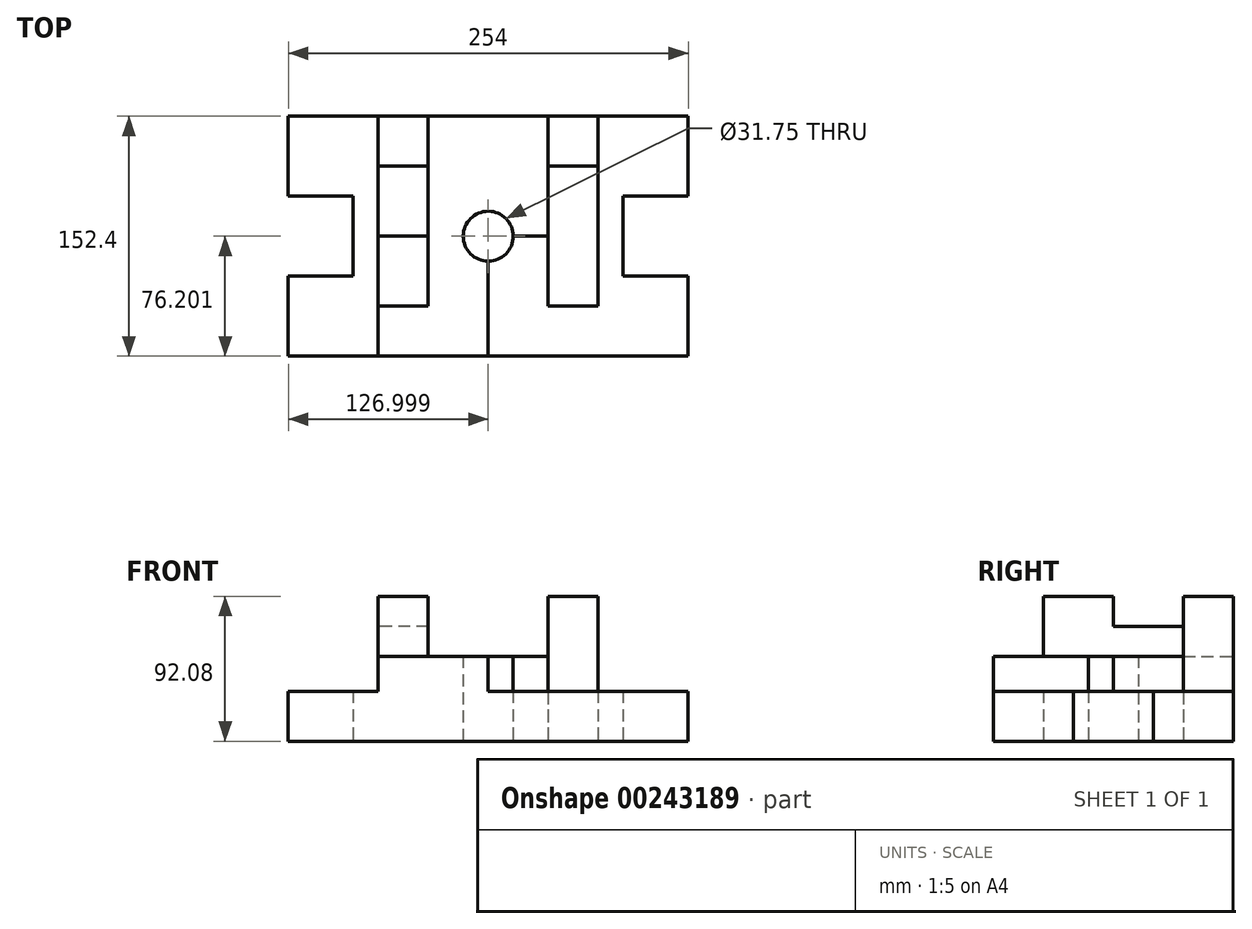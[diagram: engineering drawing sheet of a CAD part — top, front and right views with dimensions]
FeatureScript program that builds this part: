
annotation { "Feature Type Name" : "Feature", "Feature Type Description" : "" }
export const myFeature = defineFeature(function(context is Context, id is Id, definition is map)
    precondition{}
    {
        {
            var Q0;
            Q0=qCreatedBy(makeId("Top.planeOp"),FACE);
            var sketch = newSketch(context, id + "F0", { "sketchPlane" : qUnion([Q0])});
            skLineSegment(sketch, "E0.bottom", {"start": v(84.48, -54.02) * mm, "end": v(-42.52, -54.02) * mm});
            skLineSegment(sketch, "E0.top", {"start": v(84.48, -3.22) * mm, "end": v(43.2, -3.22) * mm});
            skLineSegment(sketch, "E0.left", {"start": v(84.48, -54.02) * mm, "end": v(84.48, -3.22) * mm});
            skLineSegment(sketch, "E0.right", {"start": v(-42.52, -54.02) * mm, "end": v(-42.52, -3.22) * mm});
            skLineSegment(sketch, "E1.top", {"start": v(-42.52, 22.18) * mm, "end": v(43.2, 22.18) * mm});
            skLineSegment(sketch, "E1.left", {"start": v(-42.52, -3.22) * mm, "end": v(-42.52, 22.18) * mm});
            skLineSegment(sketch, "E1.right", {"start": v(43.2, -3.22) * mm, "end": v(43.2, 22.18) * mm});
            skLineSegment(sketch, "E2.bottom", {"start": v(-42.52, -54.02) * mm, "end": v(27.33, -54.02) * mm});
            skLineSegment(sketch, "E2.top", {"start": v(-42.52, 22.18) * mm, "end": v(27.33, 22.18) * mm});
            skLineSegment(sketch, "E2.left", {"start": v(-42.52, -54.02) * mm, "end": v(-42.52, 22.18) * mm});
            skLineSegment(sketch, "E2.right", {"start": v(27.33, -54.02) * mm, "end": v(27.33, 22.18) * mm});
            skLineSegment(sketch, "E3.bottom", {"start": v(27.33, -54.02) * mm, "end": v(-4.42, -54.02) * mm});
            skLineSegment(sketch, "E3.top", {"start": v(27.33, -22.27) * mm, "end": v(-4.42, -22.27) * mm});
            skLineSegment(sketch, "E3.left", {"start": v(27.33, -54.02) * mm, "end": v(27.33, -22.27) * mm});
            skLineSegment(sketch, "E3.right", {"start": v(-4.42, -54.02) * mm, "end": v(-4.42, -22.27) * mm});
            skLineSegment(sketch, "E4.MirrorCS", {"start": v(84.48, 47.58) * mm, "end": v(43.2, 47.58) * mm});
            skLineSegment(sketch, "E5.MirrorCS", {"start": v(27.33, 66.63) * mm, "end": v(-4.42, 66.63) * mm});
            skLineSegment(sketch, "E6.MirrorCS", {"start": v(-42.52, 47.58) * mm, "end": v(-42.52, 22.18) * mm});
            skLineSegment(sketch, "E7.MirrorCS", {"start": v(-42.52, 98.38) * mm, "end": v(-42.52, 47.58) * mm});
            skLineSegment(sketch, "E8.MirrorCS", {"start": v(27.33, 98.38) * mm, "end": v(27.33, 66.63) * mm});
            skLineSegment(sketch, "E9.MirrorCS", {"start": v(-4.42, 98.38) * mm, "end": v(-4.42, 66.63) * mm});
            skLineSegment(sketch, "E10.MirrorCS", {"start": v(27.33, 98.38) * mm, "end": v(-4.42, 98.38) * mm});
            skLineSegment(sketch, "E11.MirrorCS", {"start": v(43.2, 47.58) * mm, "end": v(43.2, 22.18) * mm});
            skLineSegment(sketch, "E12.MirrorCS", {"start": v(84.48, 98.38) * mm, "end": v(-42.52, 98.38) * mm});
            skLineSegment(sketch, "E13.MirrorCS", {"start": v(27.33, 98.38) * mm, "end": v(27.33, 22.18) * mm});
            skLineSegment(sketch, "E14.MirrorCS", {"start": v(-42.52, 98.38) * mm, "end": v(27.33, 98.38) * mm});
            skLineSegment(sketch, "E15.MirrorCS", {"start": v(-42.52, 98.38) * mm, "end": v(-42.52, 22.18) * mm});
            skLineSegment(sketch, "E16.MirrorCS", {"start": v(84.48, 98.38) * mm, "end": v(84.48, 47.58) * mm});
            skLineSegment(sketch, "E17.MirrorCS", {"start": v(-169.52, 47.58) * mm, "end": v(-128.25, 47.58) * mm});
            skLineSegment(sketch, "E18.MirrorCS", {"start": v(-42.52, 22.18) * mm, "end": v(-112.37, 22.18) * mm});
            skLineSegment(sketch, "E19.MirrorCS", {"start": v(-112.37, 98.38) * mm, "end": v(-80.62, 98.38) * mm});
            skLineSegment(sketch, "E20.MirrorCS", {"start": v(-112.37, 66.63) * mm, "end": v(-80.62, 66.63) * mm});
            skLineSegment(sketch, "E21.MirrorCS", {"start": v(-42.52, 22.18) * mm, "end": v(-128.25, 22.18) * mm});
            skLineSegment(sketch, "E22.MirrorCS", {"start": v(-112.37, -54.02) * mm, "end": v(-112.37, -22.27) * mm});
            skLineSegment(sketch, "E23.MirrorCS", {"start": v(-42.52, 98.38) * mm, "end": v(-112.37, 98.38) * mm});
            skLineSegment(sketch, "E24.MirrorCS", {"start": v(-112.37, -54.02) * mm, "end": v(-112.37, 22.18) * mm});
            skLineSegment(sketch, "E25.MirrorCS", {"start": v(-169.52, 98.38) * mm, "end": v(-169.52, 47.58) * mm});
            skLineSegment(sketch, "E26.MirrorCS", {"start": v(-80.62, 98.38) * mm, "end": v(-80.62, 66.63) * mm});
            skLineSegment(sketch, "E27.MirrorCS", {"start": v(-169.52, 98.38) * mm, "end": v(-42.52, 98.38) * mm});
            skLineSegment(sketch, "E28.MirrorCS", {"start": v(-112.37, -54.02) * mm, "end": v(-80.62, -54.02) * mm});
            skLineSegment(sketch, "E29.MirrorCS", {"start": v(-112.37, 98.38) * mm, "end": v(-112.37, 22.18) * mm});
            skLineSegment(sketch, "E30.MirrorCS", {"start": v(-112.37, -22.27) * mm, "end": v(-80.62, -22.27) * mm});
            skLineSegment(sketch, "E31.MirrorCS", {"start": v(-80.62, -54.02) * mm, "end": v(-80.62, -22.27) * mm});
            skLineSegment(sketch, "E32.MirrorCS", {"start": v(-42.52, -54.02) * mm, "end": v(-112.37, -54.02) * mm});
            skLineSegment(sketch, "E33.MirrorCS", {"start": v(-169.52, -54.02) * mm, "end": v(-42.52, -54.02) * mm});
            skLineSegment(sketch, "E34.MirrorCS", {"start": v(-128.25, 47.58) * mm, "end": v(-128.25, 22.18) * mm});
            skLineSegment(sketch, "E35.MirrorCS", {"start": v(-169.52, -3.22) * mm, "end": v(-128.25, -3.22) * mm});
            skLineSegment(sketch, "E36.MirrorCS", {"start": v(-128.25, -3.22) * mm, "end": v(-128.25, 22.18) * mm});
            skLineSegment(sketch, "E37.MirrorCS", {"start": v(-169.52, -54.02) * mm, "end": v(-169.52, -3.22) * mm});
            skLineSegment(sketch, "E38.MirrorCS", {"start": v(-112.37, 98.38) * mm, "end": v(-112.37, 66.63) * mm});
            skCircle(sketch, "E39", {"center": v(-42.52, 22.18) * mm, "radius": 15.88 * mm});
            skLineSegment(sketch, "E40.left", {"start": v(-112.37, 66.63) * mm, "end": v(-112.37, -22.27) * mm});
            skLineSegment(sketch, "E40.right", {"start": v(-80.62, 66.63) * mm, "end": v(-80.62, -22.27) * mm});
            skLineSegment(sketch, "E41.bottom", {"start": v(-4.42, 66.63) * mm, "end": v(27.33, 66.63) * mm});
            skLineSegment(sketch, "E41.top", {"start": v(-4.42, -22.27) * mm, "end": v(27.33, -22.27) * mm});
            skLineSegment(sketch, "E41.left", {"start": v(-4.42, 66.63) * mm, "end": v(-4.42, -22.27) * mm});
            skLineSegment(sketch, "E41.right", {"start": v(27.33, 66.63) * mm, "end": v(27.33, -22.27) * mm});
            skSolve(sketch);
        }
        {
            var Q0;
            Q0=makeQuery(id+"F0.imprint","IMPRINT",FACE,{"disambiguationData":[TD([[makeQuery(id+"F0.imprint","IMPRINT",EDGE,{"derivedFrom":sQuery(id+"F0.wireOp",EDGE,"E3.bottom")}),-1.0]])]});
            var Q1;
            {var subQ0=sQuery(id+"F0.wireOp",EDGE,"E9.MirrorCS");Q1=makeQuery(id+"F0.imprint","IMPRINT",FACE,{"disambiguationData":[TD([[makeQuery(id+"F0.imprint","IMPRINT",EDGE,{"derivedFrom":subQ0}),1.0]])]});}
            var Q2;
            {var subQ3=sQuery(id+"F0.wireOp",EDGE,"E30.MirrorCS");Q2=makeQuery(id+"F0.imprint","IMPRINT",FACE,{"disambiguationData":[TD([[makeQuery(id+"F0.imprint","IMPRINT",EDGE,{"derivedFrom":subQ3}),-1.0]])]});}
            var Q3;
            {var subQ0=sQuery(id+"F0.wireOp",EDGE,"E26.MirrorCS");Q3=makeQuery(id+"F0.imprint","IMPRINT",FACE,{"disambiguationData":[TD([[makeQuery(id+"F0.imprint","IMPRINT",EDGE,{"derivedFrom":subQ0}),-1.0]])]});}
            var Q4;
            {var subQ1=sQuery(id+"F0.wireOp",EDGE,"E2.bottom");Q4=makeQuery(id+"F0.imprint","IMPRINT",FACE,{"disambiguationData":[TD([[makeQuery(id+"F0.imprint","IMPRINT",EDGE,{"derivedFrom":subQ1}),1.0]])]});}
            var Q5;
            {var subQ9=sQuery(id+"F0.wireOp",EDGE,"E9.MirrorCS");Q5=makeQuery(id+"F0.imprint","IMPRINT",FACE,{"disambiguationData":[TD([[makeQuery(id+"F0.imprint","IMPRINT",EDGE,{"derivedFrom":subQ9}),-1.0]])]});}
            var Q6;
            {var subQ4=sQuery(id+"F0.wireOp",EDGE,"E30.MirrorCS");Q6=makeQuery(id+"F0.imprint","IMPRINT",FACE,{"disambiguationData":[TD([[makeQuery(id+"F0.imprint","IMPRINT",EDGE,{"derivedFrom":subQ4}),1.0]])]});}
            var Q7;
            {var subQ6=sQuery(id+"F0.wireOp",EDGE,"E26.MirrorCS");Q7=makeQuery(id+"F0.imprint","IMPRINT",FACE,{"disambiguationData":[TD([[makeQuery(id+"F0.imprint","IMPRINT",EDGE,{"derivedFrom":subQ6}),1.0]])]});}
            var Q8;
            {var subQ5=sQuery(id+"F0.wireOp",EDGE,"E31.MirrorCS");Q8=makeQuery(id+"F0.imprint","IMPRINT",FACE,{"disambiguationData":[TD([[makeQuery(id+"F0.imprint","IMPRINT",EDGE,{"derivedFrom":subQ5}),-1.0]])]});}
            var Q9;
            {var subQ0=sQuery(id+"F0.wireOp",EDGE,"E24.MirrorCS");Q9=makeQuery(id+"F0.imprint","IMPRINT",FACE,{"disambiguationData":[TD([[makeQuery(id+"F0.imprint","IMPRINT",EDGE,{"derivedFrom":subQ0}),-1.0]])]});}
            extrude(context, id + "F1", {"entities" : qUnion([Q0, Q1, Q2, Q3, Q4, Q5, Q6, Q7, Q8, Q9]), "depth" : 53.97 * mm});
        }
        {
            var Q0;
            Q0 = qSketchRegion(id + "F0", true);
            var Q1;
            {var subQ5=sQuery(id+"F0.wireOp",EDGE,"E30.MirrorCS");Q1=makeQuery(id+"F0.imprint","IMPRINT",FACE,{"disambiguationData":[TD([[makeQuery(id+"F0.imprint","IMPRINT",EDGE,{"derivedFrom":subQ5}),1.0]])]});}
            var Q2;
            {var subQ5=sQuery(id+"F0.wireOp",EDGE,"E20.MirrorCS");Q2=makeQuery(id+"F0.imprint","IMPRINT",FACE,{"disambiguationData":[TD([[makeQuery(id+"F0.imprint","IMPRINT",EDGE,{"derivedFrom":subQ5}),-1.0]])]});}
            var Q3;
            {var subQ5=sQuery(id+"F0.wireOp",EDGE,"E41.bottom");Q3=makeQuery(id+"F0.imprint","IMPRINT",FACE,{"disambiguationData":[TD([[makeQuery(id+"F0.imprint","IMPRINT",EDGE,{"derivedFrom":subQ5}),-1.0]])]});}
            var Q4;
            {var subQ5=sQuery(id+"F0.wireOp",EDGE,"E41.top");Q4=makeQuery(id+"F0.imprint","IMPRINT",FACE,{"disambiguationData":[TD([[makeQuery(id+"F0.imprint","IMPRINT",EDGE,{"derivedFrom":subQ5}),1.0]])]});}
            extrude(context, id + "F2", {"entities" : qUnion([Q0, Q1, Q2, Q3, Q4]), "operationType" : NewBodyOperationType.ADD, "depth" : 31.75 * mm});
        }
        {
            var Q0;
            {var subQ5=sQuery(id+"F0.wireOp",EDGE,"E20.MirrorCS");Q0=makeQuery(id+"F0.imprint","IMPRINT",FACE,{"disambiguationData":[TD([[makeQuery(id+"F0.imprint","IMPRINT",EDGE,{"derivedFrom":subQ5}),-1.0]])]});}
            var Q1;
            {var subQ0=sQuery(id+"F0.wireOp",EDGE,"E26.MirrorCS");Q1=makeQuery(id+"F0.imprint","IMPRINT",FACE,{"disambiguationData":[TD([[makeQuery(id+"F0.imprint","IMPRINT",EDGE,{"derivedFrom":subQ0}),-1.0]])]});}
            var Q2;
            {var subQ5=sQuery(id+"F0.wireOp",EDGE,"E30.MirrorCS");Q2=makeQuery(id+"F0.imprint","IMPRINT",FACE,{"disambiguationData":[TD([[makeQuery(id+"F0.imprint","IMPRINT",EDGE,{"derivedFrom":subQ5}),1.0]])]});}
            var Q3;
            {var subQ0=sQuery(id+"F0.wireOp",EDGE,"E24.MirrorCS");Q3=makeQuery(id+"F0.imprint","IMPRINT",FACE,{"disambiguationData":[TD([[makeQuery(id+"F0.imprint","IMPRINT",EDGE,{"derivedFrom":subQ0}),-1.0]])]});}
            var Q4;
            {var subQ0=sQuery(id+"F0.wireOp",EDGE,"E9.MirrorCS");Q4=makeQuery(id+"F0.imprint","IMPRINT",FACE,{"disambiguationData":[TD([[makeQuery(id+"F0.imprint","IMPRINT",EDGE,{"derivedFrom":subQ0}),1.0]])]});}
            var Q5;
            {var subQ5=sQuery(id+"F0.wireOp",EDGE,"E41.bottom");Q5=makeQuery(id+"F0.imprint","IMPRINT",FACE,{"disambiguationData":[TD([[makeQuery(id+"F0.imprint","IMPRINT",EDGE,{"derivedFrom":subQ5}),-1.0]])]});}
            var Q6;
            {var subQ5=sQuery(id+"F0.wireOp",EDGE,"E41.top");Q6=makeQuery(id+"F0.imprint","IMPRINT",FACE,{"disambiguationData":[TD([[makeQuery(id+"F0.imprint","IMPRINT",EDGE,{"derivedFrom":subQ5}),1.0]])]});}
            var Q7;
            Q7=makeQuery(id+"F0.imprint","IMPRINT",FACE,{"disambiguationData":[TD([[makeQuery(id+"F0.imprint","IMPRINT",EDGE,{"derivedFrom":sQuery(id+"F0.wireOp",EDGE,"E3.bottom")}),-1.0]])]});
            extrude(context, id + "F3", {"entities" : qUnion([Q0, Q1, Q2, Q3, Q4, Q5, Q6, Q7]), "operationType" : NewBodyOperationType.ADD, "depth" : 73.02 * mm});
        }
        {
            var Q0;
            {var subQ0=sQuery(id+"F0.wireOp",EDGE,"E24.MirrorCS");Q0=makeQuery(id+"F0.imprint","IMPRINT",FACE,{"disambiguationData":[TD([[makeQuery(id+"F0.imprint","IMPRINT",EDGE,{"derivedFrom":subQ0}),-1.0]])]});}
            var Q1;
            {var subQ0=sQuery(id+"F0.wireOp",EDGE,"E26.MirrorCS");Q1=makeQuery(id+"F0.imprint","IMPRINT",FACE,{"disambiguationData":[TD([[makeQuery(id+"F0.imprint","IMPRINT",EDGE,{"derivedFrom":subQ0}),-1.0]])]});}
            var Q2;
            {var subQ0=sQuery(id+"F0.wireOp",EDGE,"E9.MirrorCS");Q2=makeQuery(id+"F0.imprint","IMPRINT",FACE,{"disambiguationData":[TD([[makeQuery(id+"F0.imprint","IMPRINT",EDGE,{"derivedFrom":subQ0}),1.0]])]});}
            var Q3;
            Q3=makeQuery(id+"F0.imprint","IMPRINT",FACE,{"disambiguationData":[TD([[makeQuery(id+"F0.imprint","IMPRINT",EDGE,{"derivedFrom":sQuery(id+"F0.wireOp",EDGE,"E3.bottom")}),-1.0]])]});
            extrude(context, id + "F4", {"entities" : qUnion([Q0, Q1, Q2, Q3]), "operationType" : NewBodyOperationType.ADD, "depth" : 92.07 * mm});
        }
    });
